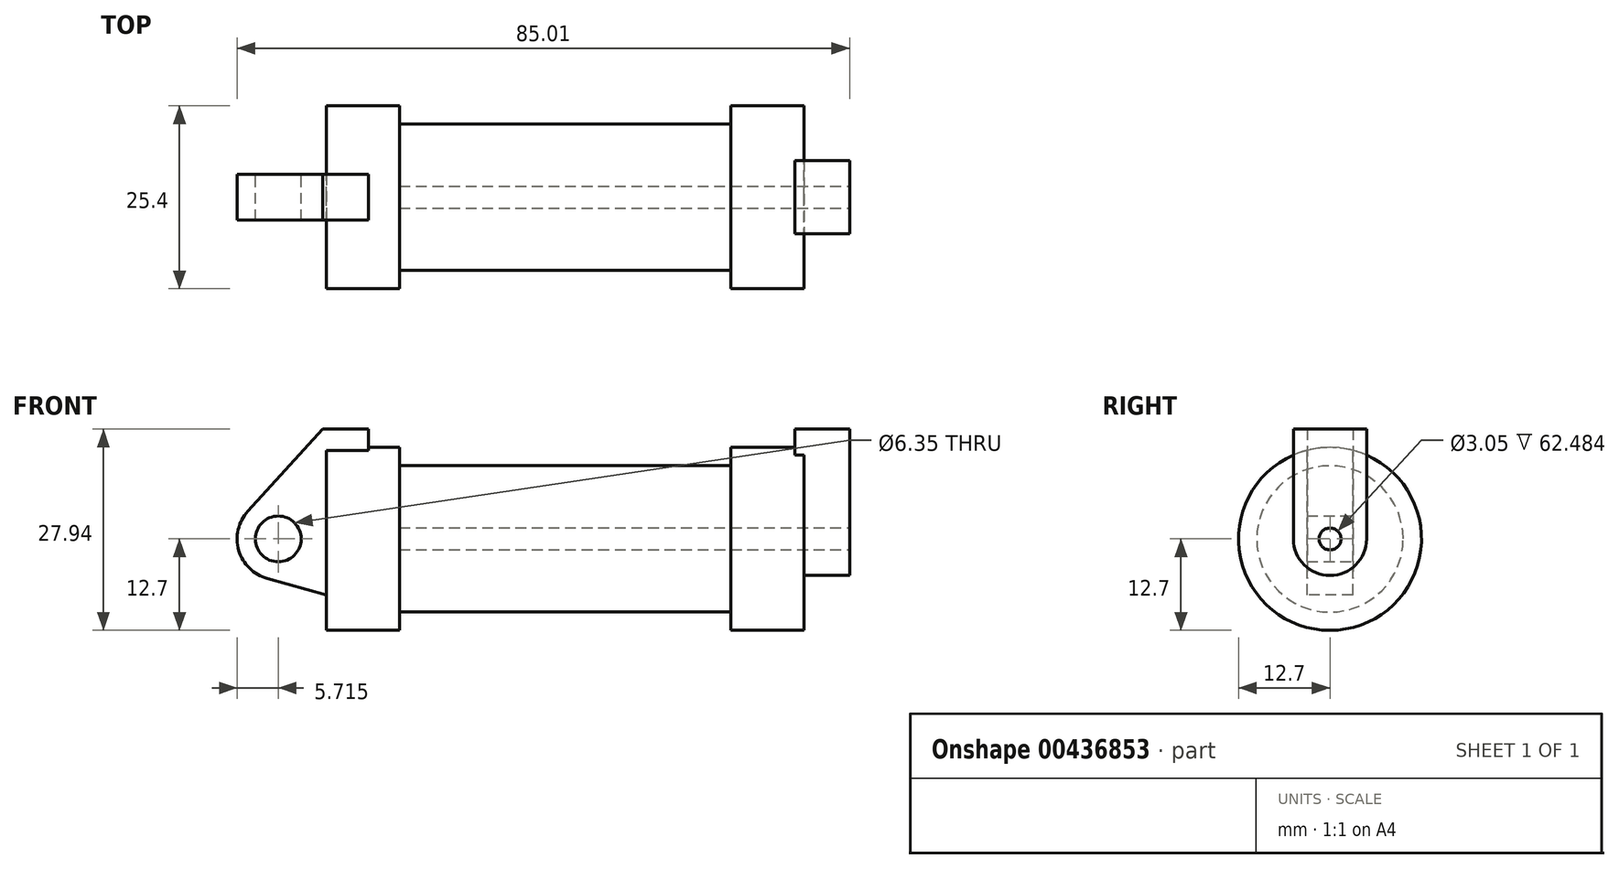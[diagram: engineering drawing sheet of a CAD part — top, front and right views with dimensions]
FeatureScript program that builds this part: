
annotation { "Feature Type Name" : "Feature", "Feature Type Description" : "" }
export const myFeature = defineFeature(function(context is Context, id is Id, definition is map)
    precondition{}
    {
        {
            var Q0;
            Q0=qCreatedBy(makeId("Front.planeOp"),FACE);
            var sketch = newSketch(context, id + "F0", { "sketchPlane" : qUnion([Q0])});
            skLineSegment(sketch, "E0", {"start": v(0, 0) * mm, "end": v(0, 12.7) * mm});
            skLineSegment(sketch, "E1", {"start": v(0, 12.7) * mm, "end": v(10.16, 12.7) * mm});
            skLineSegment(sketch, "E2", {"start": v(10.16, 12.7) * mm, "end": v(10.16, 10.16) * mm});
            skLineSegment(sketch, "E3", {"start": v(10.16, 10.16) * mm, "end": v(56.13, 10.16) * mm});
            skLineSegment(sketch, "E4", {"start": v(56.13, 10.16) * mm, "end": v(56.13, 12.7) * mm});
            skLineSegment(sketch, "E5", {"start": v(56.13, 12.7) * mm, "end": v(66.3, 12.7) * mm});
            skLineSegment(sketch, "E6", {"start": v(66.3, 12.7) * mm, "end": v(66.3, 0) * mm});
            skLineSegment(sketch, "E7", {"start": v(66.3, 0) * mm, "end": v(0, 0) * mm});
            skLineSegment(sketch, "E8", {"start": v(5.84, 15.24) * mm, "end": v(-0.5, 15.24) * mm});
            skLineSegment(sketch, "E9", {"start": v(-0.5, 15.24) * mm, "end": v(-10.88, 3.85) * mm});
            skLineSegment(sketch, "E10", {"start": v(0, 0) * mm, "end": v(-6.65, 0) * mm});
            skCircle(sketch, "E11", {"center": v(-6.65, 0) * mm, "radius": 5.72 * mm});
            skCircle(sketch, "E12", {"center": v(-6.65, 0) * mm, "radius": 3.18 * mm});
            skLineSegment(sketch, "E13", {"start": v(5.84, 15.24) * mm, "end": v(5.84, -9.4) * mm});
            skLineSegment(sketch, "E14", {"start": v(5.84, -9.4) * mm, "end": v(-8.18, -5.5) * mm});
            skSolve(sketch);
        }
        {
            var Q0;
            {var subQ1=sQuery(id+"F0.wireOp",EDGE,"E0");Q0=makeQuery(id+"F0.imprint","IMPRINT",FACE,{"disambiguationData":[TD([[makeQuery(id+"F0.imprint","IMPRINT",EDGE,{"derivedFrom":subQ1}),1.0]])]});}
            var Q1;
            {var subQ0=sQuery(id+"F0.wireOp",EDGE,"E0");Q1=makeQuery(id+"F0.imprint","IMPRINT",FACE,{"disambiguationData":[TD([[makeQuery(id+"F0.imprint","IMPRINT",EDGE,{"derivedFrom":subQ0}),-1.0]])]});}
            var Q2;
            {var subQ0=sQuery(id+"F0.wireOp",EDGE,"E14");Q2=makeQuery(id+"F0.imprint","IMPRINT",FACE,{"disambiguationData":[TD([[makeQuery(id+"F0.imprint","IMPRINT",EDGE,{"derivedFrom":subQ0}),-1.0]])]});}
            var Q3;
            {var subQ5=sQuery(id+"F0.wireOp",EDGE,"E12");Q3=makeQuery(id+"F0.imprint","IMPRINT",FACE,{"disambiguationData":[TD([[makeQuery(id+"F0.imprint","IMPRINT",EDGE,{"derivedFrom":subQ5}),-1.0]])]});}
            extrude(context, id + "F1", {"entities" : qUnion([Q0, Q1, Q2, Q3]), "endBound" : BoundingType.SYMMETRIC, "depth" : 6.35 * mm});
        }
        {
            var Q0;
            {var subQ0=sQuery(id+"F0.wireOp",EDGE,"E0");Q0=makeQuery(id+"F0.imprint","IMPRINT",FACE,{"disambiguationData":[TD([[makeQuery(id+"F0.imprint","IMPRINT",EDGE,{"derivedFrom":subQ0}),-1.0]])]});}
            var Q1;
            {var subQ0=sQuery(id+"F0.wireOp",EDGE,"E2");Q1=makeQuery(id+"F0.imprint","IMPRINT",FACE,{"disambiguationData":[TD([[makeQuery(id+"F0.imprint","IMPRINT",EDGE,{"derivedFrom":subQ0}),-1.0]])]});}
            var Q2;
            Q2=sQuery(id+"F0.wireOp",EDGE,"E7");
            revolve(context, id + "F2", {"operationType" : NewBodyOperationType.ADD, "entities" : qUnion([Q0, Q1]), "axis" : qUnion([Q2]), "revolveType" : RevolveType.FULL});
        }
        {
            var Q0;
            Q0=makeQuery(id+"F2.opRevolve","SWEPT_FACE",FACE,{"disambiguationData":[OSD([sQuery(id+"F0.wireOp",EDGE,"E6")])]});
            var sketch = newSketch(context, id + "F3", { "sketchPlane" : qUnion([Q0])});
            skCircle(sketch, "E15", {"center": v(0, 0) * mm, "radius": 5.08 * mm});
            skCircle(sketch, "E16", {"center": v(0, 0) * mm, "radius": 1.52 * mm});
            skLineSegment(sketch, "E17", {"start": v(5.08, 0) * mm, "end": v(5.08, 15.24) * mm});
            skLineSegment(sketch, "E18", {"start": v(-5.08, 0) * mm, "end": v(-5.08, 15.24) * mm});
            skLineSegment(sketch, "E19", {"start": v(5.08, 15.24) * mm, "end": v(-5.08, 15.24) * mm});
            skSolve(sketch);
        }
        {
            var Q0;
            {var subQ0=sQuery(id+"F3.wireOp",EDGE,"E19");Q0=makeQuery(id+"F3.imprint","IMPRINT",FACE,{"disambiguationData":[TD([[makeQuery(id+"F3.imprint","IMPRINT",EDGE,{"derivedFrom":subQ0}),1.0]])]});}
            var Q1;
            {var subQ0=sQuery(id+"F3.wireOp",EDGE,"E17");var subQ1=sQuery(id+"F3.wireOp",EDGE,"E15");var subQ2=makeQuery(id+"F3.imprint","INTERSECT",VERTEX,{"derivedFrom":[subQ1,subQ0]});Q1=makeQuery(id+"F3.imprint","IMPRINT",FACE,{"disambiguationData":[TD([[makeQuery(id+"F3.imprint","IMPRINT",EDGE,{"disambiguationData":[TD([[subQ2,-1.0]])],"derivedFrom":subQ1}),-1.0]])]});}
            var Q2;
            Q2=makeQuery(id+"F3.imprint","IMPRINT",FACE,{"disambiguationData":[TD([[makeQuery(id+"F3.imprint","IMPRINT",EDGE,{"derivedFrom":sQuery(id+"F3.wireOp",EDGE,"E16")}),-1.0]])]});
            extrude(context, id + "F4", {"entities" : qUnion([Q0, Q1, Q2]), "operationType" : NewBodyOperationType.ADD, "oppositeDirection" : true, "depth" : 1.27 * mm, "hasSecondDirection" : true, "secondDirectionOppositeDirection" : false, "secondDirectionDepth" : 6.35 * mm});
        }
        {
            var Q0;
            Q0=makeQuery(id+"F4.boolean.opBoolean","SPLIT",FACE,{"disambiguationData":[TD([makeQuery(id+"F4.opExtrude","SWEPT_FACE",FACE,{"disambiguationData":[OSD([sQuery(id+"F3.wireOp",EDGE,"E16")])]})])],"derivedFrom":makeQuery(id+"F2.opRevolve","SWEPT_FACE",FACE,{"disambiguationData":[OSD([sQuery(id+"F0.wireOp",EDGE,"E6")])]})});
            extrude(context, id + "F5", {"entities" : qUnion([Q0]), "operationType" : NewBodyOperationType.REMOVE, "oppositeDirection" : true, "depth" : 56.13 * mm});
        }
    });
